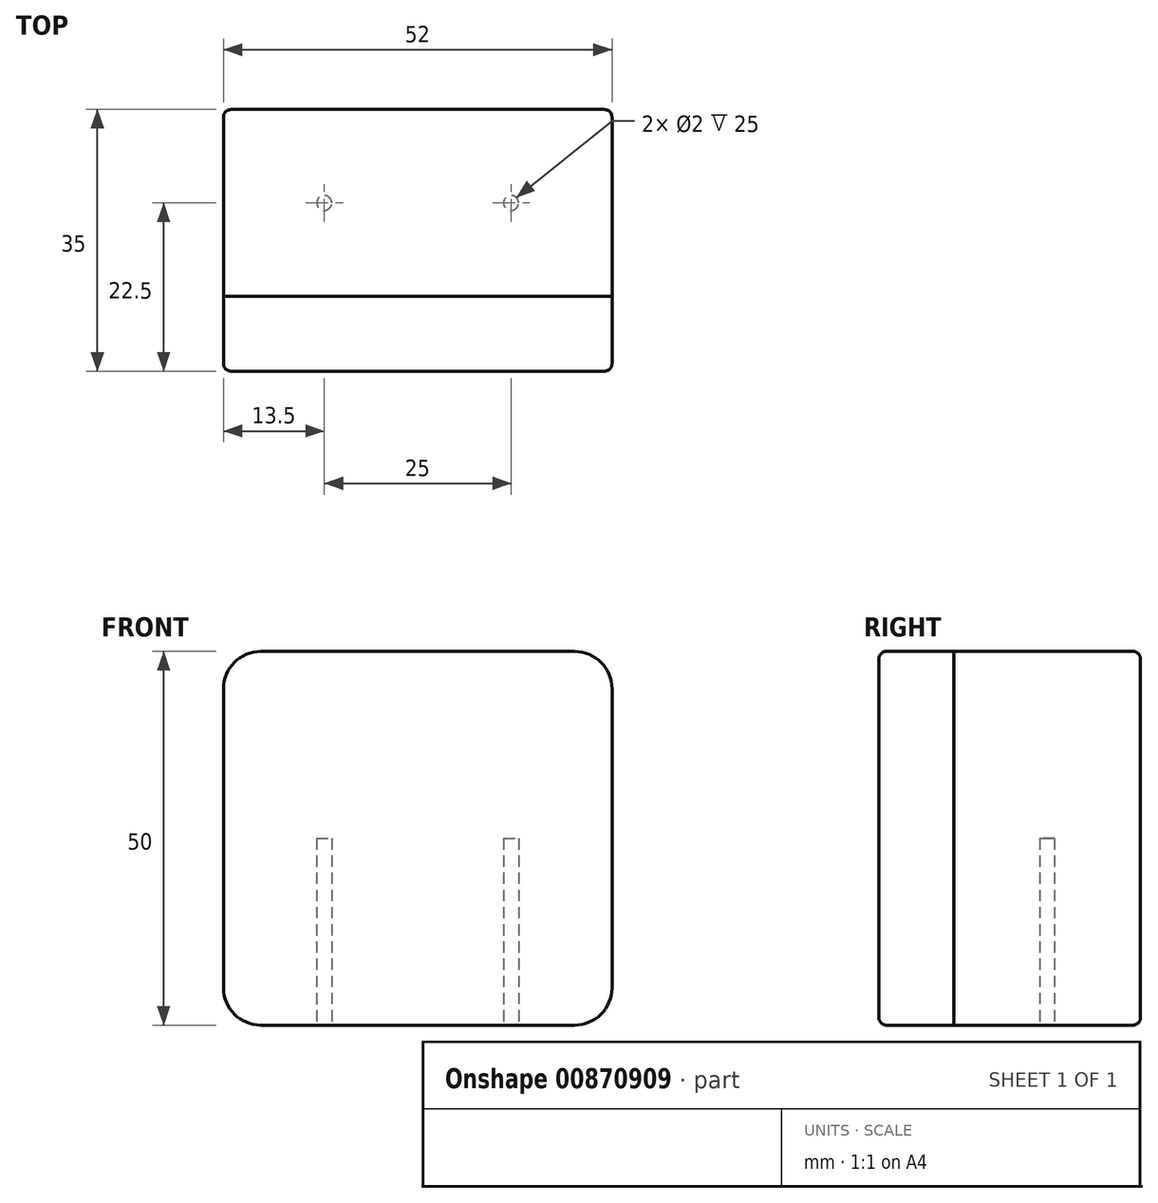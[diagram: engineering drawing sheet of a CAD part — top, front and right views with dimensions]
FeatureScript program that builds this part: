
annotation { "Feature Type Name" : "Feature", "Feature Type Description" : "" }
export const myFeature = defineFeature(function(context is Context, id is Id, definition is map)
    precondition{}
    {
        {
            var Q0;
            Q0=qCreatedBy(makeId("Front.planeOp"),FACE);
            var sketch = newSketch(context, id + "F0", { "sketchPlane" : qUnion([Q0])});
            skLineSegment(sketch, "E0.bottom", {"start": v(26, -25) * mm, "end": v(-26, -25) * mm});
            skLineSegment(sketch, "E0.top", {"start": v(26, 25) * mm, "end": v(-26, 25) * mm});
            skLineSegment(sketch, "E0.left", {"start": v(26, -25) * mm, "end": v(26, 25) * mm});
            skLineSegment(sketch, "E0.right", {"start": v(-26, -25) * mm, "end": v(-26, 25) * mm});
            skPoint(sketch, "E0.middle", {"position": v(0, 0) * mm});
            skSolve(sketch);
        }
        {
            var Q0;
            Q0 = qSketchRegion(id + "F0", true);
            extrude(context, id + "F1", {"entities" : qUnion([Q0]), "endBound" : BoundingType.SYMMETRIC, "depth" : 25 * mm, "offsetDistance" : 25 * mm});
        }
        {
            var Q0;
            Q0=makeQuery(id+"F1.opExtrude","CAP_FACE",FACE,{"disambiguationData":[OSD([sQuery(id+"F0.wireOp",EDGE,"E0.bottom"),sQuery(id+"F0.wireOp",EDGE,"E0.top"),sQuery(id+"F0.wireOp",EDGE,"E0.left"),sQuery(id+"F0.wireOp",EDGE,"E0.right")])],"isStart":false});
            extrude(context, id + "F2", {"entities" : qUnion([Q0]), "depth" : 10 * mm, "offsetDistance" : 25 * mm});
        }
        {
            var Q0;
            Q0=makeQuery(id+"F1.opExtrude","SWEPT_EDGE",EDGE,{"disambiguationData":[OSD([sQuery(id+"F0.wireOp",EDGE,"E0.top"),sQuery(id+"F0.wireOp",EDGE,"E0.left")])]});
            var Q1;
            Q1=makeQuery(id+"F1.opExtrude","SWEPT_EDGE",EDGE,{"disambiguationData":[OSD([sQuery(id+"F0.wireOp",EDGE,"E0.top"),sQuery(id+"F0.wireOp",EDGE,"E0.right")])]});
            var Q2;
            Q2=makeQuery(id+"F1.opExtrude","SWEPT_EDGE",EDGE,{"disambiguationData":[OSD([sQuery(id+"F0.wireOp",EDGE,"E0.bottom"),sQuery(id+"F0.wireOp",EDGE,"E0.left")])]});
            var Q3;
            Q3=makeQuery(id+"F1.opExtrude","SWEPT_EDGE",EDGE,{"disambiguationData":[OSD([sQuery(id+"F0.wireOp",EDGE,"E0.bottom"),sQuery(id+"F0.wireOp",EDGE,"E0.right")])]});
            var Q4;
            Q4=makeQuery(id+"F2.opExtrude","SWEPT_EDGE",EDGE,{"disambiguationData":[OSD([sQuery(id+"F0.wireOp",EDGE,"E0.top"),sQuery(id+"F0.wireOp",EDGE,"E0.left")])]});
            var Q5;
            Q5=makeQuery(id+"F2.opExtrude","SWEPT_EDGE",EDGE,{"disambiguationData":[OSD([sQuery(id+"F0.wireOp",EDGE,"E0.bottom"),sQuery(id+"F0.wireOp",EDGE,"E0.left")])]});
            var Q6;
            Q6=makeQuery(id+"F2.opExtrude","SWEPT_EDGE",EDGE,{"disambiguationData":[OSD([sQuery(id+"F0.wireOp",EDGE,"E0.top"),sQuery(id+"F0.wireOp",EDGE,"E0.right")])]});
            var Q7;
            Q7=makeQuery(id+"F2.opExtrude","SWEPT_EDGE",EDGE,{"disambiguationData":[OSD([sQuery(id+"F0.wireOp",EDGE,"E0.bottom"),sQuery(id+"F0.wireOp",EDGE,"E0.right")])]});
            fillet(context, id + "F3", {"entities" : qUnion([Q0, Q1, Q2, Q3, Q4, Q5, Q6, Q7]), "radius" : 5 * mm, "tangentPropagation" : true, "allowEdgeOverflow" : false});
        }
        {
            var Q0;
            Q0=makeQuery(id+"F1.opExtrude","CAP_FACE",FACE,{"disambiguationData":[OSD([sQuery(id+"F0.wireOp",EDGE,"E0.bottom"),sQuery(id+"F0.wireOp",EDGE,"E0.top"),sQuery(id+"F0.wireOp",EDGE,"E0.left"),sQuery(id+"F0.wireOp",EDGE,"E0.right")])],"isStart":true});
            var Q1;
            Q1=makeQuery(id+"F2.opExtrude","CAP_FACE",FACE,{"disambiguationData":[OSD([sQuery(id+"F0.wireOp",EDGE,"E0.bottom"),sQuery(id+"F0.wireOp",EDGE,"E0.top"),sQuery(id+"F0.wireOp",EDGE,"E0.left"),sQuery(id+"F0.wireOp",EDGE,"E0.right")])],"isStart":false});
            fillet(context, id + "F4", {"entities" : qUnion([Q0, Q1]), "radius" : 1 * mm, "tangentPropagation" : true, "allowEdgeOverflow" : false});
        }
        {
            var Q0;
            Q0=makeQuery(id+"F1.opExtrude","SWEPT_FACE",FACE,{"disambiguationData":[OSD([sQuery(id+"F0.wireOp",EDGE,"E0.bottom")])]});
            var sketch = newSketch(context, id + "F5", { "sketchPlane" : qUnion([Q0])});
            skCircle(sketch, "E1", {"center": v(-12.5, 0) * mm, "radius": 1 * mm});
            skCircle(sketch, "E2.MirrorC", {"center": v(12.5, 0) * mm, "radius": 1 * mm});
            skSolve(sketch);
        }
        {
            var Q0;
            Q0 = qSketchRegion(id + "F5", true);
            extrude(context, id + "F6", {"entities" : qUnion([Q0]), "operationType" : NewBodyOperationType.REMOVE, "oppositeDirection" : true, "depth" : 25 * mm, "offsetDistance" : 25 * mm});
        }
    });
